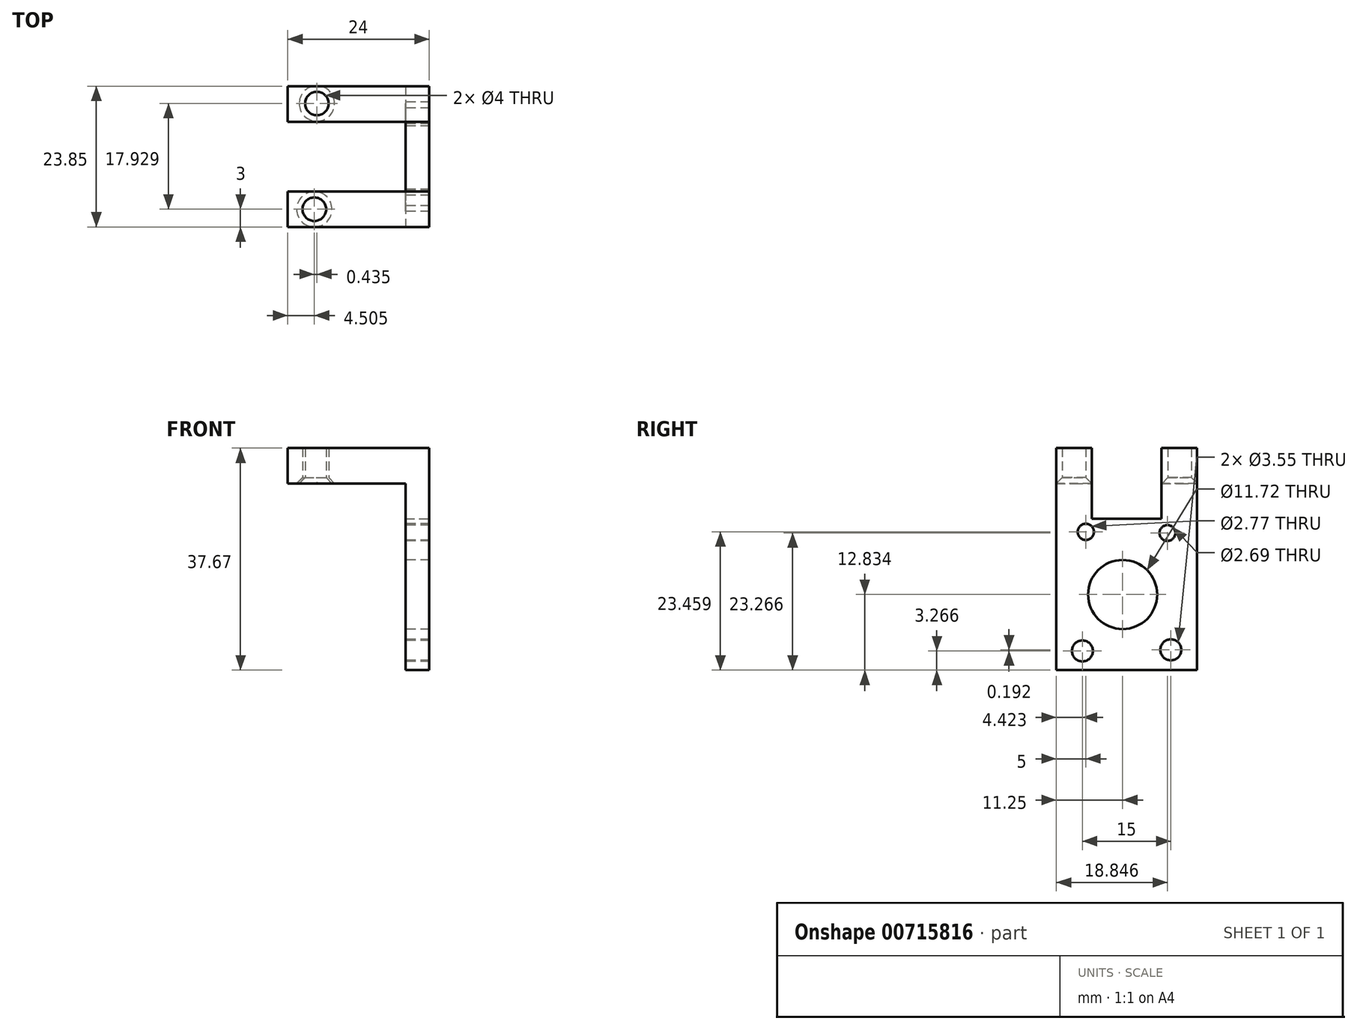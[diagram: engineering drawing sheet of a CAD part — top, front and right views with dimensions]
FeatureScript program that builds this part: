
annotation { "Feature Type Name" : "Feature", "Feature Type Description" : "" }
export const myFeature = defineFeature(function(context is Context, id is Id, definition is map)
    precondition{}
    {
        {
            var Q0;
            Q0=qCreatedBy(makeId("Right.planeOp"),FACE);
            var sketch = newSketch(context, id + "F0", { "sketchPlane" : qUnion([Q0])});
            skLineSegment(sketch, "E0.bottom", {"start": v(-11.25, 0) * mm, "end": v(12.6, 0) * mm});
            skLineSegment(sketch, "E0.top", {"start": v(-11.25, -25.67) * mm, "end": v(12.6, -25.67) * mm});
            skLineSegment(sketch, "E0.left", {"start": v(-11.25, 0) * mm, "end": v(-11.25, -25.67) * mm});
            skLineSegment(sketch, "E0.right", {"start": v(12.6, 0) * mm, "end": v(12.6, -25.67) * mm});
            skCircle(sketch, "E1", {"center": v(0, -12.84) * mm, "radius": 5.86 * mm});
            skPoint(sketch, "E1.centerSnap0", {"position": v(-11.25, -12.84) * mm});
            skCircle(sketch, "E2", {"center": v(-6.25, -2.21) * mm, "radius": 1.39 * mm});
            skCircle(sketch, "E3", {"center": v(7.6, -2.4) * mm, "radius": 1.35 * mm});
            skCircle(sketch, "E4", {"center": v(-6.83, -22.4) * mm, "radius": 1.77 * mm});
            skCircle(sketch, "E5", {"center": v(8.17, -22.21) * mm, "radius": 1.77 * mm});
            skSolve(sketch);
        }
        {
            var Q0;
            Q0 = qSketchRegion(id + "F0", true);
            extrude(context, id + "F1", {"entities" : qUnion([Q0]), "depth" : 4 * mm, "offsetDistance" : 25 * mm});
        }
        {
            var Q0;
            Q0=makeQuery(id+"F1.opExtrude","SWEPT_FACE",FACE,{"disambiguationData":[OSD([sQuery(id+"F0.wireOp",EDGE,"E0.bottom")])]});
            var sketch = newSketch(context, id + "F2", { "sketchPlane" : qUnion([Q0])});
            skLineSegment(sketch, "E6.bottom", {"start": v(4, 12.6) * mm, "end": v(0, 12.6) * mm});
            skLineSegment(sketch, "E6.top", {"start": v(4, 6.6) * mm, "end": v(0, 6.6) * mm});
            skLineSegment(sketch, "E6.left", {"start": v(4, 12.6) * mm, "end": v(4, 6.6) * mm});
            skLineSegment(sketch, "E6.right", {"start": v(0, 12.6) * mm, "end": v(0, 6.6) * mm});
            skLineSegment(sketch, "E7.bottom", {"start": v(0, -11.25) * mm, "end": v(4, -11.25) * mm});
            skLineSegment(sketch, "E7.top", {"start": v(0, -5.25) * mm, "end": v(4, -5.25) * mm});
            skLineSegment(sketch, "E7.left", {"start": v(0, -11.25) * mm, "end": v(0, -5.25) * mm});
            skLineSegment(sketch, "E7.right", {"start": v(4, -11.25) * mm, "end": v(4, -5.25) * mm});
            skSolve(sketch);
        }
        {
            var Q0;
            Q0 = qSketchRegion(id + "F2", true);
            extrude(context, id + "F3", {"entities" : qUnion([Q0]), "operationType" : NewBodyOperationType.ADD, "depth" : 10 * mm, "offsetDistance" : 25 * mm});
        }
        {
            var Q0;
            Q0=makeQuery(id+"F3.opExtrude","CAP_FACE",FACE,{"disambiguationData":[OSD([sQuery(id+"F2.wireOp",EDGE,"E6.bottom"),sQuery(id+"F2.wireOp",EDGE,"E6.top"),sQuery(id+"F2.wireOp",EDGE,"E6.left"),sQuery(id+"F2.wireOp",EDGE,"E6.right")])],"isStart":false});
            var Q1;
            Q1=makeQuery(id+"F3.opExtrude","CAP_FACE",FACE,{"disambiguationData":[OSD([sQuery(id+"F2.wireOp",EDGE,"E7.bottom"),sQuery(id+"F2.wireOp",EDGE,"E7.top"),sQuery(id+"F2.wireOp",EDGE,"E7.left"),sQuery(id+"F2.wireOp",EDGE,"E7.right")])],"isStart":false});
            extrude(context, id + "F4", {"entities" : qUnion([Q0, Q1]), "operationType" : NewBodyOperationType.ADD, "depth" : 2 * mm, "offsetDistance" : 25 * mm});
        }
        {
            var Q0;
            {var subQ0=sQuery(id+"F2.wireOp",EDGE,"E7.left");var subQ1=sQuery(id+"F2.wireOp",EDGE,"E6.right");Q0=makeQuery(id+"F4.boolean.opBoolean","MERGE",FACE,{"derivedFrom":[makeQuery(id+"F3.boolean.opBoolean","MERGE",FACE,{"derivedFrom":[makeQuery(id+"F1.opExtrude","CAP_FACE",FACE,{"disambiguationData":[OSD([sQuery(id+"F0.wireOp",EDGE,"E0.bottom"),sQuery(id+"F0.wireOp",EDGE,"E0.top"),sQuery(id+"F0.wireOp",EDGE,"E0.left"),sQuery(id+"F0.wireOp",EDGE,"E0.right"),sQuery(id+"F0.wireOp",EDGE,"E1"),sQuery(id+"F0.wireOp",EDGE,"E2"),sQuery(id+"F0.wireOp",EDGE,"E3"),sQuery(id+"F0.wireOp",EDGE,"E4"),sQuery(id+"F0.wireOp",EDGE,"E5")])],"isStart":true}),makeQuery(id+"F3.opExtrude","SWEPT_FACE",FACE,{"disambiguationData":[OSD([subQ1])]}),makeQuery(id+"F3.opExtrude","SWEPT_FACE",FACE,{"disambiguationData":[OSD([subQ0])]})]}),makeQuery(id+"F4.opExtrude","SWEPT_FACE",FACE,{"disambiguationData":[OSD([subQ1])]}),makeQuery(id+"F4.opExtrude","SWEPT_FACE",FACE,{"disambiguationData":[OSD([subQ0])]})]});}
            var sketch = newSketch(context, id + "F5", { "sketchPlane" : qUnion([Q0])});
            skLineSegment(sketch, "E8.bottom", {"start": v(-12.6, 12) * mm, "end": v(-6.6, 12) * mm});
            skLineSegment(sketch, "E8.top", {"start": v(-12.6, 6) * mm, "end": v(-6.6, 6) * mm});
            skLineSegment(sketch, "E8.left", {"start": v(-12.6, 12) * mm, "end": v(-12.6, 6) * mm});
            skLineSegment(sketch, "E8.right", {"start": v(-6.6, 12) * mm, "end": v(-6.6, 6) * mm});
            skLineSegment(sketch, "E9.bottom", {"start": v(5.25, 12) * mm, "end": v(11.25, 12) * mm});
            skLineSegment(sketch, "E9.top", {"start": v(5.25, 6) * mm, "end": v(11.25, 6) * mm});
            skLineSegment(sketch, "E9.left", {"start": v(5.25, 12) * mm, "end": v(5.25, 6) * mm});
            skLineSegment(sketch, "E9.right", {"start": v(11.25, 12) * mm, "end": v(11.25, 6) * mm});
            skSolve(sketch);
        }
        {
            var Q0;
            Q0 = qSketchRegion(id + "F5", true);
            extrude(context, id + "F6", {"entities" : qUnion([Q0]), "operationType" : NewBodyOperationType.ADD, "depth" : 20 * mm, "offsetDistance" : 25 * mm});
        }
        {
            var Q0;
            Q0=makeQuery(id+"F6.opExtrude","SWEPT_FACE",FACE,{"disambiguationData":[OSD([sQuery(id+"F5.wireOp",EDGE,"E9.top")])]});
            var sketch = newSketch(context, id + "F7", { "sketchPlane" : qUnion([Q0])});
            skPoint(sketch, "E10", {"position": v(-15.5, 8.25) * mm});
            skPoint(sketch, "E10.positionSnap0", {"position": v(-20, 8.25) * mm});
            skPoint(sketch, "E11", {"position": v(-15.06, -9.68) * mm});
            skSolve(sketch);
        }
        {
            var Q0;
            Q0=sQuery(id+"F7.wireOp",VERTEX,"E10");
            var Q1;
            Q1=makeQuery(id+"F1.opExtrude","SWEPT_BODY",BODY,{"disambiguationData":[OSD([sQuery(id+"F0.wireOp",EDGE,"E0.bottom"),sQuery(id+"F0.wireOp",EDGE,"E0.top"),sQuery(id+"F0.wireOp",EDGE,"E0.left"),sQuery(id+"F0.wireOp",EDGE,"E0.right"),sQuery(id+"F0.wireOp",EDGE,"E1"),sQuery(id+"F0.wireOp",EDGE,"E2"),sQuery(id+"F0.wireOp",EDGE,"E3"),sQuery(id+"F0.wireOp",EDGE,"E4"),sQuery(id+"F0.wireOp",EDGE,"E5")])]});
            hole(context, id + "F8", {"style" : HoleStyle.C_SINK, "endStyle" : HoleEndStyle.THROUGH, "holeDiameter" : 4 * mm, "cSinkDiameter" : 6 * mm, "cSinkAngle" : 90 * degree, "majorDiameter" : 5 * mm, "isTappedThrough" : true, "tappedDepth" : 12 * mm, "tapClearance" : 3, "locations" : qUnion([Q0]), "scope" : qUnion([Q1])});
        }
        {
            var Q0;
            Q0=sQuery(id+"F7.wireOp",VERTEX,"E11");
            var Q1;
            Q1=makeQuery(id+"F1.opExtrude","SWEPT_BODY",BODY,{"disambiguationData":[OSD([sQuery(id+"F0.wireOp",EDGE,"E0.bottom"),sQuery(id+"F0.wireOp",EDGE,"E0.top"),sQuery(id+"F0.wireOp",EDGE,"E0.left"),sQuery(id+"F0.wireOp",EDGE,"E0.right"),sQuery(id+"F0.wireOp",EDGE,"E1"),sQuery(id+"F0.wireOp",EDGE,"E2"),sQuery(id+"F0.wireOp",EDGE,"E3"),sQuery(id+"F0.wireOp",EDGE,"E4"),sQuery(id+"F0.wireOp",EDGE,"E5")])]});
            hole(context, id + "F9", {"style" : HoleStyle.C_SINK, "endStyle" : HoleEndStyle.THROUGH, "holeDiameter" : 4 * mm, "cSinkDiameter" : 6 * mm, "cSinkAngle" : 90 * degree, "majorDiameter" : 5 * mm, "isTappedThrough" : true, "tappedDepth" : 12 * mm, "tapClearance" : 3, "locations" : qUnion([Q0]), "scope" : qUnion([Q1])});
        }
    });
